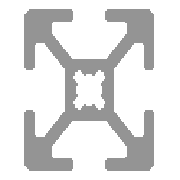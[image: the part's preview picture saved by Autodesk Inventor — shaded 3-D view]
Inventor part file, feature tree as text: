
AUTODESK INVENTOR PART (.ipt)
format: ipt  version: 2017 (Build 210142000, 142)  size: 232,960 bytes
history: native  units: in
note: dims shown in document units (in); Inventor stores cm internally (conversion verified against a paired STEP export)
features: other x3, sketch x1
ambient origin geometry x8: Origin, YZ Plane, XZ Plane, XY Plane, X Axis, Y Axis, Z Axis, Center Point
bodies: Solid1 (feature_tree), Body (feature_tree)
feature tree (4):
  other  "Blocks"
  other  "Start Plane"
  other  "End Plane"
  sketch  "Sketch1"  dims[d2=-0.0in d3=1.0in d4=72.0in d5=0.0in d7=1.0in]
